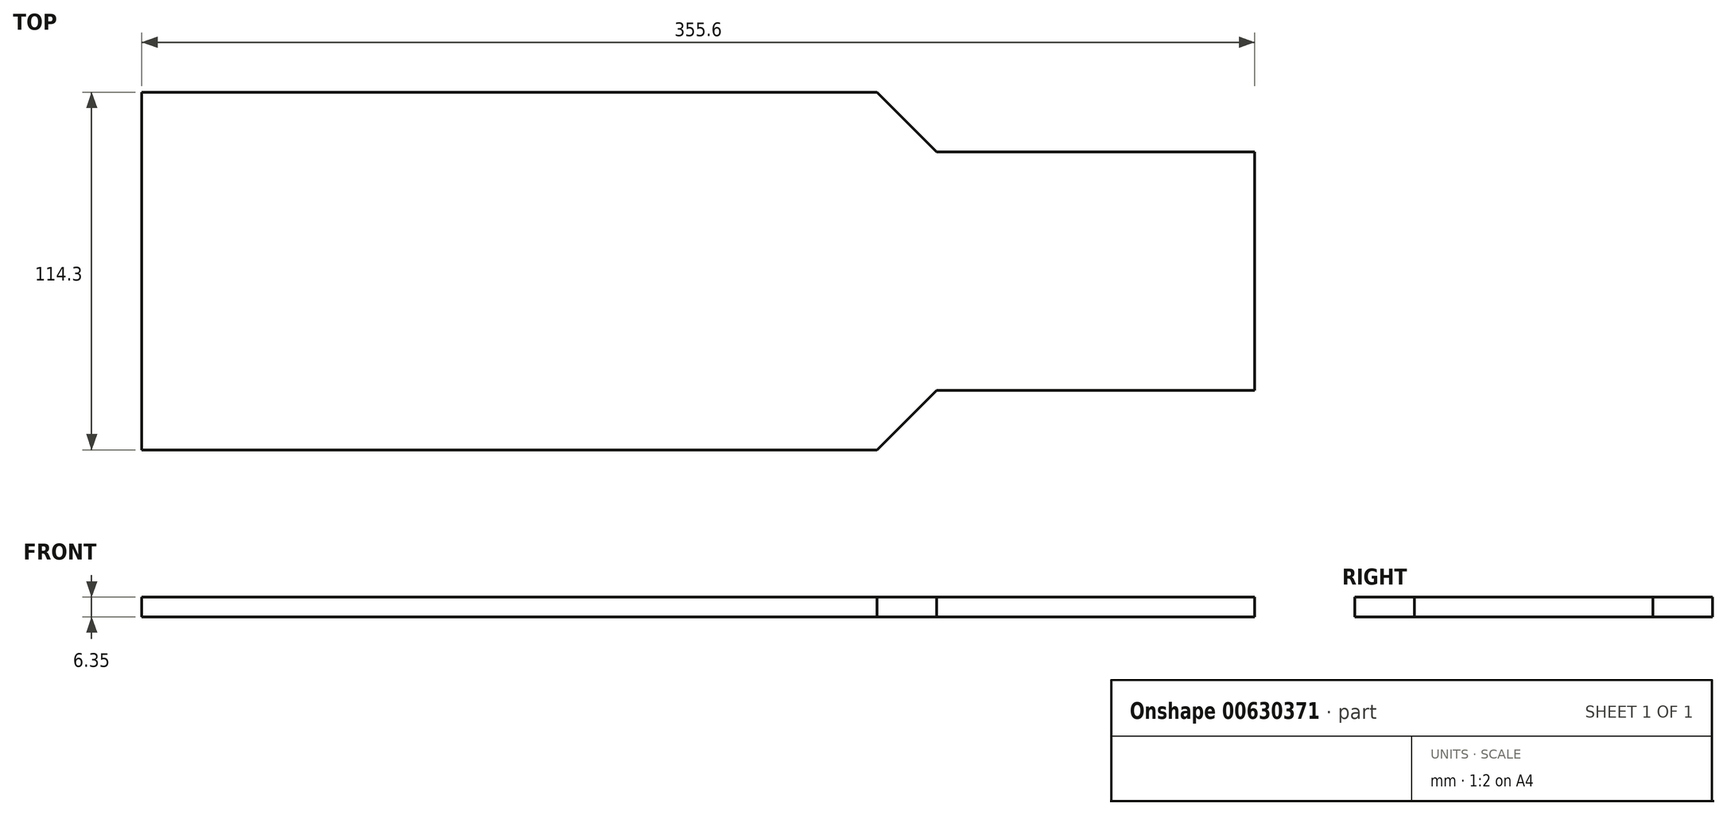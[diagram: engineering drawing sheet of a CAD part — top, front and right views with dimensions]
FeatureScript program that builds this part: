
annotation { "Feature Type Name" : "Feature", "Feature Type Description" : "" }
export const myFeature = defineFeature(function(context is Context, id is Id, definition is map)
    precondition{}
    {
        {
            var Q0;
            Q0=qCreatedBy(makeId("Top.planeOp"),FACE);
            var sketch = newSketch(context, id + "F0", { "sketchPlane" : qUnion([Q0])});
            skLineSegment(sketch, "E0.bottom", {"start": v(-101.6, 38.1) * mm, "end": v(0, 38.1) * mm});
            skLineSegment(sketch, "E0.top", {"start": v(-101.6, -38.1) * mm, "end": v(0, -38.1) * mm});
            skLineSegment(sketch, "E0.left", {"start": v(-101.6, 38.1) * mm, "end": v(-101.6, -38.1) * mm, "construction": true});
            skLineSegment(sketch, "E0.right", {"start": v(0, 38.1) * mm, "end": v(0, -38.1) * mm});
            skPoint(sketch, "E1", {"position": v(0, 0) * mm});
            skLineSegment(sketch, "E2", {"start": v(-120.65, 57.15) * mm, "end": v(-355.6, 57.15) * mm});
            skLineSegment(sketch, "E3", {"start": v(-355.6, 57.15) * mm, "end": v(-355.6, -57.15) * mm});
            skLineSegment(sketch, "E4", {"start": v(-355.6, -57.15) * mm, "end": v(-120.65, -57.15) * mm});
            skLineSegment(sketch, "E5", {"start": v(-120.65, -57.15) * mm, "end": v(-101.6, -38.1) * mm});
            skLineSegment(sketch, "E6", {"start": v(-101.6, 38.1) * mm, "end": v(-120.65, 57.15) * mm});
            skLineSegment(sketch, "E7", {"start": v(-120.65, 57.15) * mm, "end": v(-101.6, 57.15) * mm, "construction": true});
            skLineSegment(sketch, "E8", {"start": v(-101.6, 57.15) * mm, "end": v(-101.6, 38.1) * mm, "construction": true});
            skLineSegment(sketch, "E9", {"start": v(-120.65, 57.15) * mm, "end": v(-120.65, -57.15) * mm, "construction": true});
            skSolve(sketch);
        }
        {
            var Q0;
            Q0 = qSketchRegion(id + "F0", true);
            extrude(context, id + "F1", {"entities" : qUnion([Q0]), "depth" : 6.35 * mm, "offsetDistance" : 25.4 * mm});
        }
        {
            var Q0;
            Q0=makeQuery(id+"F1.opExtrude","CAP_FACE",FACE,{"disambiguationData":[OSD([sQuery(id+"F0.wireOp",EDGE,"E0.bottom"),sQuery(id+"F0.wireOp",EDGE,"E0.top"),sQuery(id+"F0.wireOp",EDGE,"E0.right"),sQuery(id+"F0.wireOp",EDGE,"E2"),sQuery(id+"F0.wireOp",EDGE,"E3"),sQuery(id+"F0.wireOp",EDGE,"E4"),sQuery(id+"F0.wireOp",EDGE,"E5"),sQuery(id+"F0.wireOp",EDGE,"E6")])],"isStart":false});
            var Q1;
            Q1=makeQuery(id+"F1.opExtrude","CAP_EDGE",EDGE,{"disambiguationData":[OSD([sQuery(id+"F0.wireOp",EDGE,"E3")])],"isStart":false});
            cPlane(context, id + "F2", {"entities" : qUnion([Q0, Q1]), "cplaneType" : CPlaneType.LINE_ANGLE, "offset" : 25.4 * mm, "angle" : 15 * degree, "width" : 152.4 * mm, "height" : 152.4 * mm});
        }
    });
